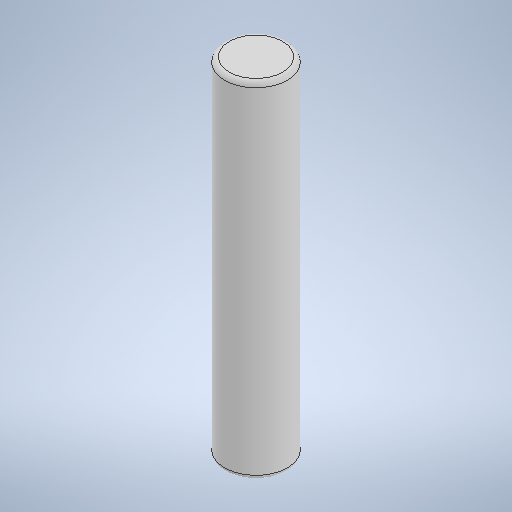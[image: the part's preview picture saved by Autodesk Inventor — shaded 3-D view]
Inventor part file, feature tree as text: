
AUTODESK INVENTOR PART (.ipt)
format: ipt  version: 2025.1 (Build 291241000, 241)  size: 261,120 bytes
history: native  units: mm
features: extrude x1, fillet x1, sketch x1
ambient origin geometry x8: Origin, YZ Plane, XZ Plane, XY Plane, X Axis, Y Axis, Z Axis, Center Point
bodies: Solid1 (feature_tree)
feature tree (3):
  extrude  "Extrusion1"  Depth=11.0mm TaperAngle=0.0deg
  fillet  "Fillet1"  Radius=0.15mm
  sketch  "Sketch1"  dims[d0=2.0mm d1=11.0mm d2=0.0mm d3=0.15mm]
